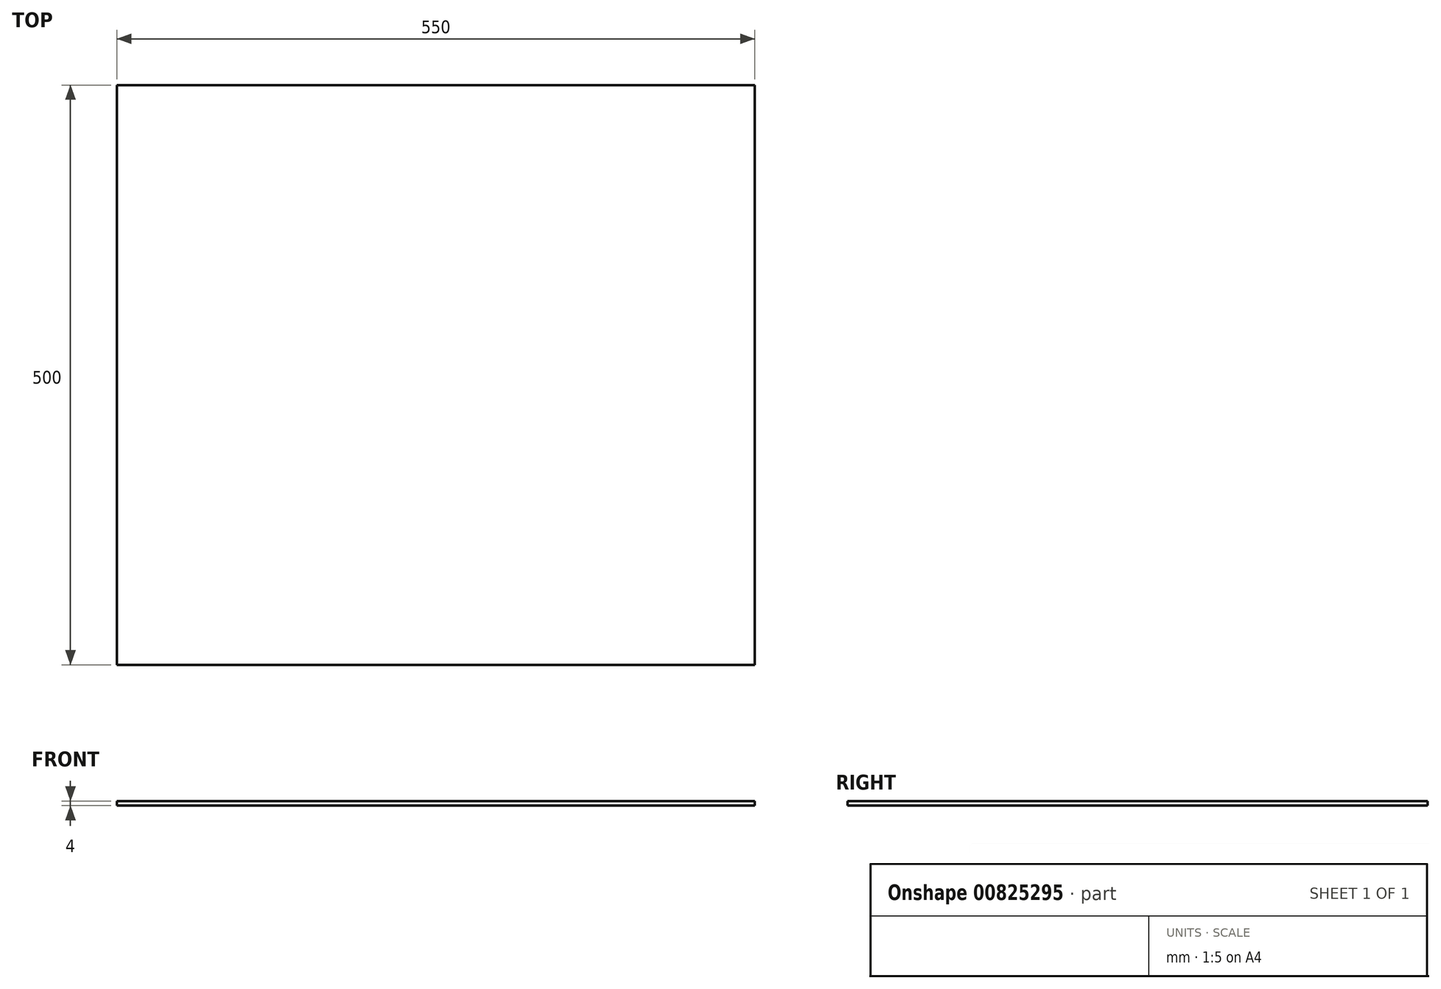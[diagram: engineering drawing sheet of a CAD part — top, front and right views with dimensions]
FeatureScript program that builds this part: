
annotation { "Feature Type Name" : "Feature", "Feature Type Description" : "" }
export const myFeature = defineFeature(function(context is Context, id is Id, definition is map)
    precondition{}
    {
        {
            assignVariable(context, id + "F0", {"name" : "glass_W", "anyValue" : 4});
        }
        {
            var Q0;
            Q0=qCreatedBy(makeId("Top.planeOp"),FACE);
            var sketch = newSketch(context, id + "F1", { "sketchPlane" : qUnion([Q0])});
            skLineSegment(sketch, "E0.bottom", {"start": v(-275, 250) * mm, "end": v(275, 250) * mm});
            skLineSegment(sketch, "E0.top", {"start": v(-275, -250) * mm, "end": v(275, -250) * mm});
            skLineSegment(sketch, "E0.left", {"start": v(-275, 250) * mm, "end": v(-275, -250) * mm});
            skLineSegment(sketch, "E0.right", {"start": v(275, 250) * mm, "end": v(275, -250) * mm});
            skPoint(sketch, "E0.middle", {"position": v(0, 0) * mm});
            skSolve(sketch);
        }
        {
            var Q0;
            Q0=makeQuery(id+"F1.imprint","IMPRINT",FACE,{"disambiguationData":[TD([[makeQuery(id+"F1.imprint","IMPRINT",EDGE,{"derivedFrom":sQuery(id+"F1.wireOp",EDGE,"E0.bottom")}),-1.0]])]});
            extrude(context, id + "F2", {"entities" : qUnion([Q0]), "depth" : (getVariable(context, 'glass_W')) * mm, "offsetDistance" : 25 * mm});
        }
    });
